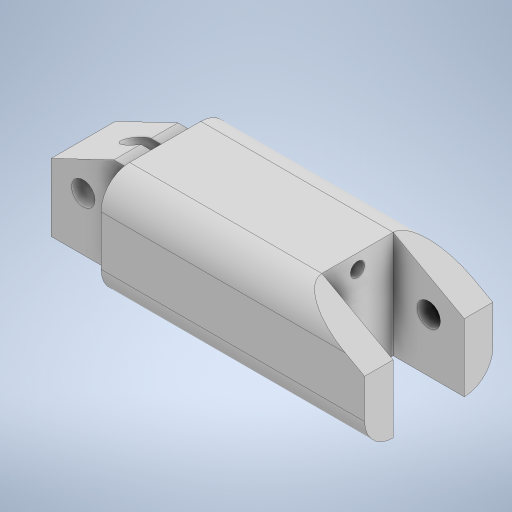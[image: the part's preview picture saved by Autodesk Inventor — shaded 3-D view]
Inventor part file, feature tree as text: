
AUTODESK INVENTOR PART (.ipt)
format: ipt  version: 2024 (Build 280153000, 153)  size: 488,448 bytes
history: native  units: mm
features: sketch x27, extrude x22, plane x5, chamfer x3, move_body x3, split x2, boolean_combine x2, fillet x1
ambient origin geometry x8: Origin, YZ Plane, XZ Plane, XY Plane, X Axis, Y Axis, Z Axis, Center Point
bodies: Solid1 (feature_tree), Solid2 (feature_tree), Solid3 (feature_tree), Solid4 (feature_tree), Solid5 (feature_tree)
feature tree (65):
  extrude  "Extrusion1"  Depth=16.0mm
  sketch  "Sketch2"  dims[d2=15.0mm d3=0.0mm d4=10.0mm]
  extrude  "Extrusion2"  Depth=10.0mm
  chamfer  "Chamfer1"  Distance=21.25mm
  extrude  "Extrusion3"  Depth=10.0mm TaperAngle=0.0deg
  extrude  "Extrusion4"  Depth=11.5mm TaperAngle=0.0deg
  extrude  "Extrusion5"  Depth=1.0mm TaperAngle=0.0deg
  chamfer  "Chamfer2"  Distance=6.0mm Angle=45.0deg
  sketch  "Sketch6"  dims[d14=7.0mm d15=11.5mm d16=0.0mm]
  extrude  "Extrusion6"  Depth=9.0mm
  extrude  "Extrusion7"  Depth=11.5mm TaperAngle=0.0deg
  chamfer  "Chamfer3"  Distance=11.5mm Angle=45.0deg
  sketch  "Sketch9"  dims[d26=3.3mm d27=45.25mm d28=0.0mm d29=11.5mm d30=5.5mm d31=45.0deg]
  extrude  "Extrusion8"  Depth=65.75mm TaperAngle=0.0deg
  extrude  "Extrusion9"  Depth=9.0mm TaperAngle=0.0deg
  extrude  "Extrusion10"  Depth=13.0mm TaperAngle=0.0deg
  sketch  "Sketch13"  dims[d43=24.0mm d44=21.0mm d45=0.0mm]
  extrude  "Extrusion11"  Depth=21.0mm TaperAngle=0.0deg
  extrude  "Extrusion12"  TaperAngle=0.0deg  [1 undecoded]
  extrude  "Extrusion13"  Depth=6.0mm TaperAngle=0.0deg
  plane  "Work Plane1"
  split  "Split1"
  move_body  "Move Body1"
  extrude  "Extrusion14"  Depth=0.5mm TaperAngle=0.0deg
  move_body  "Move Body2"
  extrude  "Extrusion15"  Depth=3.0mm
  sketch  "Sketch19"  dims[d70=31.0mm d71=29.5mm d72=0.0mm]
  sketch  "Sketch20"  dims[d76=-5.0mm d77=0.0mm d78=0.0mm d95=26.0mm d96=0.0mm]
  extrude  "Extrusion16"  Depth=1.0mm
  extrude  "Extrusion18"  Depth=29.5mm TaperAngle=0.0deg
  extrude  "Extrusion19"  Depth=26.0mm TaperAngle=0.0deg
  plane  "Work Plane5"
  sketch  "Sketch23"  dims[d101=4.0mm]
  plane  "Work Plane7"
  sketch  "Sketch24"
  extrude  "Extrusion20"  Depth=1.0mm TaperAngle=0.0deg
  plane  "Work Plane2"
  boolean_combine  "Combine1"
  split  "Split2"
  plane  "Work Plane6"
  move_body  "Move Body3"
  boolean_combine  "Combine2"
  extrude  "Extrusion27"  [1 undecoded]
  sketch  "Sketch33"
  extrude  "Extrusion28"  [1 undecoded]
  extrude  "Extrusion29"  [1 undecoded]
  fillet  "Fillet3"  [1 undecoded]
  sketch  "Sketch1"  dims[d0=36.0mm d1=16.0mm]
  sketch  "Sketch3"  dims[d5=10.0mm]
  sketch  "Sketch4"  dims[d6=3.3mm d7=21.25mm d8=0.0mm]
  sketch  "Sketch5"  dims[d9=10.0mm d10=5.5mm d11=45.0deg d12=10.0mm d13=0.0mm]
  sketch  "Sketch7"  dims[d17=3.3mm d18=1.0mm d19=0.0mm d20=6.0mm d21=11.5mm d22=45.0deg]
  sketch  "Sketch8"  dims[d23=15.0mm d24=0.0mm d25=9.0mm]
  sketch  "Sketch10"  dims[d32=2.0mm d33=65.75mm d34=0.0mm]
  sketch  "Sketch11"  dims[d35=0.5mm d36=0.0mm d37=9.0mm d38=0.0mm]
  sketch  "Sketch12"  dims[d39=0.5mm d40=0.0mm d41=13.0mm d42=0.0mm]
  sketch  "Sketch14"  dims[d46=12.25mm d47=-12.0mm d48=0.0mm d49=0.0mm]
  sketch  "Sketch15"  dims[d50=30.0mm d51=0.0mm d52=6.0mm d53=0.0mm d54=0.0mm]
  sketch  "Sketch16"  dims[d56=0.5mm d57=0.0mm d58=0.5mm d59=0.0mm]
  sketch  "Sketch17"  dims[d64=10.0mm d65=0.0mm d66=3.0mm]
  sketch  "Sketch18"  dims[d67=10.0mm d68=0.0mm d69=1.0mm]
  sketch  "Sketch22"  dims[d97=1.0mm d98=0.0mm d99=1.0mm d100=0.0mm]
  sketch  "Sketch25"
  sketch  "Sketch32"
  sketch  "Sketch34"
note: 5 required parameter values undecoded (feature->parameter linkage not recoverable at this tier; creation-order binding heuristic only, values carry confidence <= 0.55)
